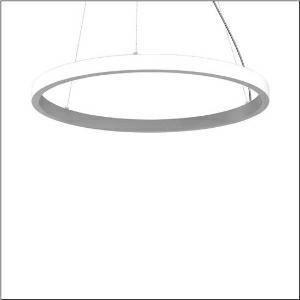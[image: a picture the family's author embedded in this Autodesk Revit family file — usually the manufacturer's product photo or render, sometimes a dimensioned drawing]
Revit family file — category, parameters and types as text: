
# Revit family: silica_r__21_ring-o_5pjbo4d1204a_97b4
name_source: partatom
category: Lighting Fixtures
units: mm (PartAtom-declared; Revit-internal decimal feet)

## family parameters
Cut with Voids When Loaded = No
Host = Face
Light Source = No
Part Type = Normal
Room Calculation Point = No
Round Connector Dimension = Use Diameter
Shared = No

## types (1)
- Silica® 21 Ring-O (1 x LED, 8820 lm, 343 W, 3000K)
    Apparent Load = 343 VA
    CIE Flux Codes = 2 16 49 50 100
    Color Rendering = 80
    Color Temperature = 3000K
    Default Elevation = 1800 mm
    Description = Silica® 21 Ring-O, suspended luminaire, of PMMA, frosted, light emission: outer ring side luminous distribution, primary light characteristic: symmetric, installation type: suspended mounting, LED, rated luminous flux: 8.820lm, luminous efficacy: 63lm/W, light colour: 830, colour temperature: 3000K, control gear: DALI 2, with terminal, 5-pole, mains connection: 230V, AC/DC, 0/50..60Hz, rated input power: 140W, housing, of extruded aluminium section, metallic grey (RAL 9006), diameter: 1.480mm, ceiling canopy, metallic grey (RAL 9006), protection rating (lamp compartment): IP40, insulation class (complete): insulation class I (protective earthing), certification: CE, impact resistance: IK02, permissible operating ambient temperature: 0..+35°C, packaging unit: 1 piece
    Height = 48 mm  [stored 0.15748 ft]
    Lamp = 1 x LED
    Lamp Light Flux = 8820 lm
    Lamp Power = 343 W
    Lamp count = 1
    Length = 1480 mm
    Luminous efficacy = 26 lm/W
    Manufacturer = Siteco
    ModVariant = No
    Model = 5PJBO4D1204A
    Mounting Place = Ceiling
    Mounting Type = Pendant
    Number of Poles = 1
    OnlyDefault = Yes
    Power Factor = 1
    Product Name = Silica® 21 Ring-O
    Product group = suspended luminaire
    ProductGroupID = 905
    Protection Class = Protection class I
    Protection Degree = IP 40
    RLX_Detail_Level = 1
    RLX_Emergency_Light_Flux = 0 lm
    RLX_Emergency_Type = 0
    RLX_Emergency_Type_DB = No
    RlxData = <blob elided: 18429 chars, md5=e3a42893>
    Socket = socket
    Standby Power = 0 W
    System Light Flux = 8819 lm
    System Power = 343 W
    Type Comments = Product without accessories
    Type Image = l_1251764.jpg
    URL = http://relux.com
    VarID = ---
    Voltage = 0 V
    Weight = 0.00 kg
    Width = 0 mm  [stored 0 ft]

note: [stored X ft] marks values corroborated as IEEE doubles in the binary element streams (Revit-internal decimal feet)

## geometry (parser evidence)
native form markers: Blend x4, Sweep x12
no freeform markers — native parametric forms only
